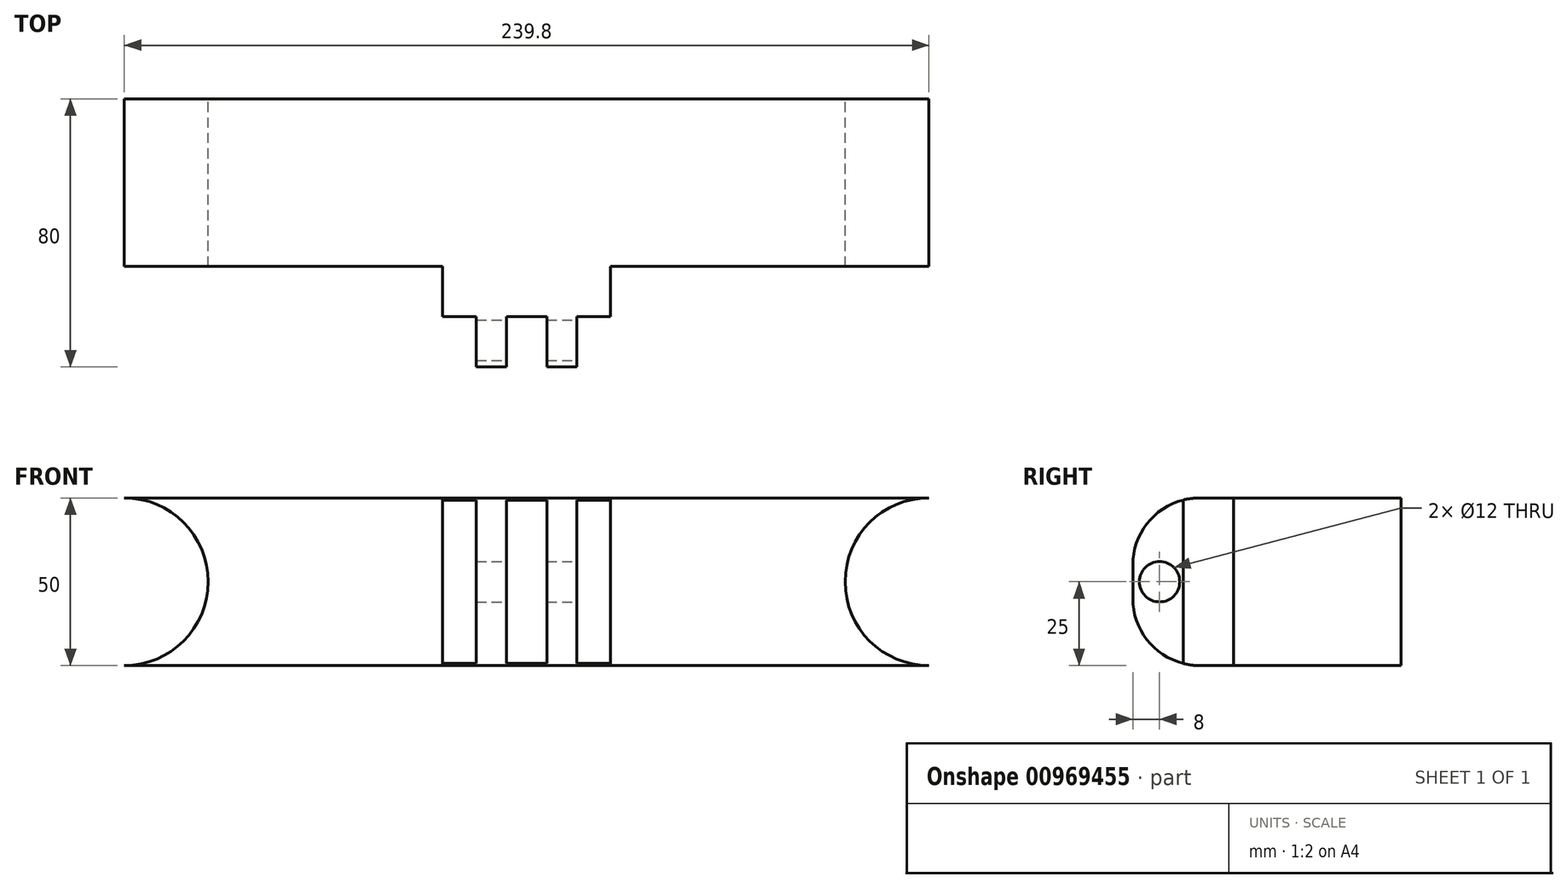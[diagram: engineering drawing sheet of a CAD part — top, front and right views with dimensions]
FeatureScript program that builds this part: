
annotation { "Feature Type Name" : "Feature", "Feature Type Description" : "" }
export const myFeature = defineFeature(function(context is Context, id is Id, definition is map)
    precondition{}
    {
        {
            var Q0;
            Q0=qCreatedBy(makeId("Front.planeOp"),FACE);
            var sketch = newSketch(context, id + "F0", { "sketchPlane" : qUnion([Q0])});
            skLineSegment(sketch, "E0.bottom", {"start": v(119.9, -25) * mm, "end": v(-119.9, -25) * mm});
            skLineSegment(sketch, "E0.top", {"start": v(119.9, 25) * mm, "end": v(-119.9, 25) * mm});
            skLineSegment(sketch, "E0.left", {"start": v(119.9, -25) * mm, "end": v(119.9, 25) * mm});
            skLineSegment(sketch, "E0.right", {"start": v(-119.9, -25) * mm, "end": v(-119.9, 25) * mm});
            skPoint(sketch, "E0.middle", {"position": v(0, 0) * mm});
            skArc(sketch, "E1", {"start": v(119.9, 25) * mm, "mid": v(94.9, 0) * mm, "end": v(119.9, -25) * mm});
            skArc(sketch, "E2", {"start": v(-119.9, 25) * mm, "mid": v(-94.9, 0) * mm, "end": v(-119.9, -25) * mm});
            skSolve(sketch);
        }
        {
            var Q0;
            Q0=makeQuery(id+"F0.imprint","IMPRINT",FACE,{"disambiguationData":[TD([[makeQuery(id+"F0.imprint","IMPRINT",EDGE,{"derivedFrom":sQuery(id+"F0.wireOp",EDGE,"E0.bottom")}),-1.0]])]});
            extrude(context, id + "F1", {"entities" : qUnion([Q0]), "endBound" : BoundingType.SYMMETRIC, "depth" : 50 * mm, "offsetDistance" : 25 * mm});
        }
        {
            var Q0;
            Q0=makeQuery(id+"F1.opExtrude","CAP_FACE",FACE,{"disambiguationData":[OSD([sQuery(id+"F0.wireOp",EDGE,"E0.bottom"),sQuery(id+"F0.wireOp",EDGE,"E0.top"),sQuery(id+"F0.wireOp",EDGE,"E1"),sQuery(id+"F0.wireOp",EDGE,"E2")])],"isStart":false});
            var sketch = newSketch(context, id + "F2", { "sketchPlane" : qUnion([Q0])});
            skLineSegment(sketch, "E3.bottom", {"start": v(25, -25) * mm, "end": v(-25, -25) * mm});
            skLineSegment(sketch, "E3.top", {"start": v(25, 25) * mm, "end": v(-25, 25) * mm});
            skLineSegment(sketch, "E3.left", {"start": v(25, -25) * mm, "end": v(25, 25) * mm});
            skLineSegment(sketch, "E3.right", {"start": v(-25, -25) * mm, "end": v(-25, 25) * mm});
            skPoint(sketch, "E3.middle", {"position": v(0, 0) * mm});
            skSolve(sketch);
        }
        {
            var Q0;
            Q0=makeQuery(id+"F2.imprint","IMPRINT",FACE,{"disambiguationData":[TD([[makeQuery(id+"F2.imprint","IMPRINT",EDGE,{"derivedFrom":sQuery(id+"F2.wireOp",EDGE,"E3.bottom")}),-1.0]])]});
            extrude(context, id + "F3", {"entities" : qUnion([Q0]), "operationType" : NewBodyOperationType.ADD, "depth" : 30 * mm, "offsetDistance" : 25 * mm});
        }
        {
            var Q0;
            Q0=makeQuery(id+"F3.boolean.opBoolean","MERGE",FACE,{"derivedFrom":[makeQuery(id+"F1.opExtrude","SWEPT_FACE",FACE,{"disambiguationData":[OSD([sQuery(id+"F0.wireOp",EDGE,"E0.bottom")])]}),makeQuery(id+"F3.opExtrude","SWEPT_FACE",FACE,{"disambiguationData":[OSD([sQuery(id+"F2.wireOp",EDGE,"E3.bottom")])]})]});
            var sketch = newSketch(context, id + "F4", { "sketchPlane" : qUnion([Q0])});
            skLineSegment(sketch, "E4", {"start": v(-25, 40) * mm, "end": v(25, 40) * mm});
            skLineSegment(sketch, "E5", {"start": v(0, 40) * mm, "end": v(0, 55) * mm});
            skLineSegment(sketch, "E6", {"start": v(-15, 55) * mm, "end": v(-15, 40) * mm});
            skLineSegment(sketch, "E7", {"start": v(15, 55) * mm, "end": v(15, 40) * mm});
            skSolve(sketch);
        }
        {
            var Q0;
            {var subQ0=sQuery(id+"F4.wireOp",EDGE,"E5");Q0=makeQuery(id+"F4.imprint","IMPRINT",FACE,{"disambiguationData":[TD([[makeQuery(id+"F4.imprint","IMPRINT",EDGE,{"derivedFrom":subQ0}),-1.0]])]});}
            var sketch = newSketch(context, id + "F5", { "sketchPlane" : qUnion([Q0])});
            skLineSegment(sketch, "E8.bottom", {"start": v(6, 40) * mm, "end": v(-6, 40) * mm});
            skLineSegment(sketch, "E8.top", {"start": v(6, 55) * mm, "end": v(-6, 55) * mm});
            skLineSegment(sketch, "E8.left", {"start": v(6, 40) * mm, "end": v(6, 55) * mm});
            skLineSegment(sketch, "E8.right", {"start": v(-6, 40) * mm, "end": v(-6, 55) * mm});
            skPoint(sketch, "E8.middle", {"position": v(0, 47.5) * mm});
            skSolve(sketch);
        }
        {
            var Q0;
            {var subQ0=sQuery(id+"F4.wireOp",EDGE,"E5");Q0=makeQuery(id+"F4.imprint","IMPRINT",FACE,{"disambiguationData":[TD([[makeQuery(id+"F4.imprint","IMPRINT",EDGE,{"derivedFrom":subQ0}),1.0]])]});}
            var sketch = newSketch(context, id + "F6", { "sketchPlane" : qUnion([Q0])});
            skLineSegment(sketch, "E9.bottom", {"start": v(-6, 55) * mm, "end": v(0, 55) * mm});
            skLineSegment(sketch, "E9.top", {"start": v(-6, 40) * mm, "end": v(0, 40) * mm});
            skLineSegment(sketch, "E9.left", {"start": v(-6, 55) * mm, "end": v(-6, 40) * mm});
            skLineSegment(sketch, "E9.right", {"start": v(0, 55) * mm, "end": v(0, 40) * mm});
            skSolve(sketch);
        }
        {
            var Q0;
            Q0=makeQuery(id+"F6.imprint","IMPRINT",FACE,{"disambiguationData":[TD([[makeQuery(id+"F6.imprint","IMPRINT",EDGE,{"derivedFrom":sQuery(id+"F6.wireOp",EDGE,"E9.bottom")}),1.0]])]});
            var Q1;
            {var subQ3=sQuery(id+"F5.wireOp",EDGE,"E8.left");Q1=makeQuery(id+"F5.imprint","IMPRINT",FACE,{"disambiguationData":[TD([[makeQuery(id+"F5.imprint","IMPRINT",EDGE,{"derivedFrom":subQ3}),1.0]])]});}
            var Q2;
            {var subQ4=sQuery(id+"F4.wireOp",EDGE,"E7");Q2=makeQuery(id+"F4.imprint","IMPRINT",FACE,{"disambiguationData":[TD([[makeQuery(id+"F4.imprint","IMPRINT",EDGE,{"derivedFrom":subQ4}),1.0]])]});}
            var Q3;
            {var subQ4=sQuery(id+"F4.wireOp",EDGE,"E6");Q3=makeQuery(id+"F4.imprint","IMPRINT",FACE,{"disambiguationData":[TD([[makeQuery(id+"F4.imprint","IMPRINT",EDGE,{"derivedFrom":subQ4}),-1.0]])]});}
            extrude(context, id + "F7", {"entities" : qUnion([Q0, Q1, Q2, Q3]), "operationType" : NewBodyOperationType.REMOVE, "endBound" : BoundingType.THROUGH_ALL, "oppositeDirection" : true, "depth" : 25 * mm, "offsetDistance" : 25 * mm});
        }
        {
            var Q0;
            {var subQ0=sQuery(id+"F2.wireOp",EDGE,"E3.bottom");Q0=makeQuery(id+"F7.boolean.opBoolean","SPLIT",EDGE,{"disambiguationData":[TD([makeQuery(id+"F7.opExtrude","SWEPT_FACE",FACE,{"disambiguationData":[OSD([sQuery(id+"F4.wireOp",EDGE,"E7")])]})])],"derivedFrom":makeQuery(id+"F3.opExtrude","CAP_EDGE",EDGE,{"disambiguationData":[OSD([subQ0])],"isStart":false})});}
            var Q1;
            {var subQ0=sQuery(id+"F2.wireOp",EDGE,"E3.bottom");Q1=makeQuery(id+"F7.boolean.opBoolean","SPLIT",EDGE,{"disambiguationData":[TD([makeQuery(id+"F7.opExtrude","SWEPT_FACE",FACE,{"disambiguationData":[OSD([sQuery(id+"F4.wireOp",EDGE,"E6")])]})])],"derivedFrom":makeQuery(id+"F3.opExtrude","CAP_EDGE",EDGE,{"disambiguationData":[OSD([subQ0])],"isStart":false})});}
            var Q2;
            {var subQ0=sQuery(id+"F2.wireOp",EDGE,"E3.top");Q2=makeQuery(id+"F7.boolean.opBoolean","SPLIT",EDGE,{"disambiguationData":[TD([makeQuery(id+"F7.opExtrude","SWEPT_FACE",FACE,{"disambiguationData":[OSD([sQuery(id+"F4.wireOp",EDGE,"E6")])]})])],"derivedFrom":makeQuery(id+"F3.opExtrude","CAP_EDGE",EDGE,{"disambiguationData":[OSD([subQ0])],"isStart":false})});}
            var Q3;
            {var subQ0=sQuery(id+"F2.wireOp",EDGE,"E3.top");Q3=makeQuery(id+"F7.boolean.opBoolean","SPLIT",EDGE,{"disambiguationData":[TD([makeQuery(id+"F7.opExtrude","SWEPT_FACE",FACE,{"disambiguationData":[OSD([sQuery(id+"F4.wireOp",EDGE,"E7")])]})])],"derivedFrom":makeQuery(id+"F3.opExtrude","CAP_EDGE",EDGE,{"disambiguationData":[OSD([subQ0])],"isStart":false})});}
            fillet(context, id + "F8", {"entities" : qUnion([Q0, Q1, Q2, Q3]), "radius" : 20 * mm, "tangentPropagation" : true, "allowEdgeOverflow" : false});
        }
        {
            var Q0;
            Q0=makeQuery(id+"F7.boolean.opBoolean","COPY",FACE,{"derivedFrom":makeQuery(id+"F7.opExtrude","SWEPT_FACE",FACE,{"disambiguationData":[OSD([sQuery(id+"F4.wireOp",EDGE,"E7")])]})});
            var sketch = newSketch(context, id + "F9", { "sketchPlane" : qUnion([Q0])});
            skCircle(sketch, "E10", {"center": v(-47, 0) * mm, "radius": 6 * mm});
            skSolve(sketch);
        }
        {
            var Q0;
            Q0 = qSketchRegion(id + "F9", true);
            extrude(context, id + "F10", {"entities" : qUnion([Q0]), "operationType" : NewBodyOperationType.REMOVE, "endBound" : BoundingType.THROUGH_ALL, "oppositeDirection" : true, "depth" : 25 * mm, "offsetDistance" : 25 * mm});
        }
    });
